# Revit family: Electronics_Loudspeaker_Bose-Professional_Designmax_DM5C
name_source: partatom
category: Communication Devices
revit_build: Autodesk Revit 2015 (Build: 20140905_0730(x64)
units: mm (PartAtom-declared; Revit-internal decimal feet)

## types (2) — shared parameters
Assembly Code = D5030
Bracket Material = Metal-Bose-Aluminium
Crossover = 1.5 kHz (passive 2-way crossover)
Default Elevation = 1219 mm
Depth = 303 mm
Description = Premium sound to maximize any design.
DesignMax loudspeakers bring outstanding audio and aesthetics to any commercial space. With 12 models to choose from, it’s easy to create tailored solutions that deliver instantly impressive sound. QuickHold mounting mechanisms make installation efficient, reducing strain and hassle — and saving substantial time. And with both black and white versions available, DesignMax loudspeakers integrate seamlessly with any décor.

The 50-watt DesignMax DM5C loudspeaker features a two-way 5.25-inch woofer and 1-inch tweeter coaxially mounted within the Dispersion Alignment system, producing a frequency range of 60 Hz - 20 kHz. The DM5C is ceiling-mounted and installs easily via QuickHold mounting arms.

FEATURES
Combine models to complete any design, big or small — 12 loudspeakers to mix and match, from 2-inch, low-profile models to 8-inch, high-SPL compression-driver loudspeakers and outdoor-rated options

Deliver instantly impressive sound with custom Bose drivers — no DSP or EQ required. For even better sound, use select Bose DSPs and amplifiers to enable Bose loudspeaker EQ and SmartBass processing, which expands performance and response at any listening level

Ensure a consistent listening experience throughout the room with the Dispersion Alignment system, which matches the coverage of the woofer to the pattern of the tweeter

Blend into any room design with elegant form factors, minimum-bezel grilles available in black or white, and removable logos

Reduce installation time with the patented QuickHold mounting system, which also reduces strain, hassle, and the chance of product damage

Install easily — all models include Euroblock connectors; ceiling-mounted models include plenum-rated backcans, tile-bridges, and front-access audio wiring that makes installation and troubleshooting easier

Applications
Performing arts venues
Places of worship
Conference centers
Retail stores
Restaurants and bars
Hospitality venues
Diameter = 202 mm
Edition number = 1
Environmental = indoor only
Frequency Range = 60 to 20000 Hz
Frequency Response = 70 to 17000 Hz
HF Driver = 1 x 1-inch (25 mm) neodymium dome tweeter, coaxially mounted, weather-treated
Height = 0 mm
Keynote = 16700
LF Driver = 1 x 5.25-inch woofer (133 mm), weather treated
Manufacturer = BOSE Professional
Maximum Ceiling Thickness = 0 mm
Model = DesignMax DM5C
Mounting/Suspension = Three (3) QuickHold, spring-loaded mounting arms plus three (3) safety cable tabs
Nominal Coverage Pattern = Conical
Nominal Impedance = 8 Ω
Nominal Sensitivity = Bose Extended Lifecycle Test: 88 dB; AES Transducer Test: Free field  88 dB;
Operating Temperature Range = 0 to 50 °C (32 °F to 122 °F)
Power Connector = Euroblock 6-pin connector with loop-through, front-baffle mounted. Accepts 18 AWG (0.8 mm2) to 14 AWG (2.5 mm2) size wire
Power Handling(Long-term continuous) = Bose Extended Lifecycle Test: 50W; AES Transducer Test: 60W
Power Handling(peak) = Bose Extended Lifecycle Test: 200W; AES Transducer Test: 240W
Product Guid = 25c2e7c1-eb69-4eb5-a345-2f8631cf0846
Product data url = https://www.bimobject.com
Rated Maximum SPL = Calculated max. SPL @ 1 m (Bose power test) -  105 dB ; Calculated max. SPL @ 1 m (2-hour power test) -  106 dB; Calculated max. SPL @ 1 m (Bose power test), peak -  111 dB; Calculated max. SPL @ 1 m (2-hour power test), peak - 112 dB;
Recommended High-pass Filter = 60 Hz with minimum 12 dB / octave filter
Safety Agency = UL-1480A, S5591/ UL Listed, in compliance with UL2043 for plenum-space installation, NFPA70 & NFPA90-A, in accordance with IEC60268-5, ROHS, CE compliant
Transformer Taps Information = 70V: 3, 6, 12, 25, 50 W, bypass, 100V: 6, 12, 25, 50 W, bypass
URL = https://www.bose.com
Weight = 0.00 kg
Width = 0 mm
Wire/ Conduit Entry = Single top wire entry point knockouts, allows for 9.5 mm (3/8”) conduit

## per-type parameters (varying)
| type | Mesh Material | Product code | Speaker Material |
| DM5C-Black | Grill-Bose-Black | 829683-0110 | Metal-Bose-Black |
| DM5C-White | Grill-Bose-White | 829683-0210 | Metal-Bose-White |

## geometry (parser evidence)
native form markers: Blend x16, Sweep x11
no freeform markers — native parametric forms only
